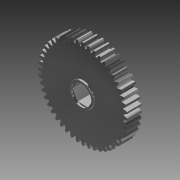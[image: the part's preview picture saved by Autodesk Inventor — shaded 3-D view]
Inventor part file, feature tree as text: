
AUTODESK INVENTOR PART (.ipt)
format: ipt  version: 2014 (Build 180170000, 170)  size: 368,640 bytes
history: native  units: mm (DEFAULTED — no unit token found)
features: plane x4, sketch x4, extrude x3, other x3, fillet x1, mirror x1
ambient origin geometry x8: Origin, YZ Plane, XZ Plane, XY Plane, X Axis, Y Axis, Z Axis, Center Point
bodies: Solid1 (feature_tree)
feature tree (16):
  extrude  "Extrusion1"  Depth=10.16mm TaperAngle=0.0deg
  plane  "Work Plane1"
  plane  "Work Plane2"
  plane  "Work Plane3"
  other  "Spur Gear"
  extrude  "Extrusion2"  Depth=76.2mm TaperAngle=0.0deg
  extrude  "Extrusion3"  TaperAngle=0.0deg  [1 undecoded]
  fillet  "Fillet1"  Radius=62.23mm
  plane  "Work Plane4"
  mirror  "Mirror1"
  sketch  "Sketch1"  dims[d0=63.5mm d1=10.16mm d2=0.0mm]
  sketch  "Sketch2"  dims[d3=60.96mm d4=76.2mm d5=0.0mm]
  other  "Srf1"
  sketch  "Sketch3"  dims[d6=0.0mm d7=0.654498mm d9=0.0mm d14=0.0mm d15=62.23mm]
  sketch  "Sketch4"  dims[d16=0.0mm d17=0.0mm d18=0.0mm d19=62.23mm d20=12.7mm d21=25.4mm d22=0.0mm d23=1.27mm d24=0.0mm d25=0.635mm]
  other  "Pitch Diameter"
note: 1 required parameter value undecoded (feature->parameter linkage not recoverable at this tier; creation-order binding heuristic only, values carry confidence <= 0.55)
